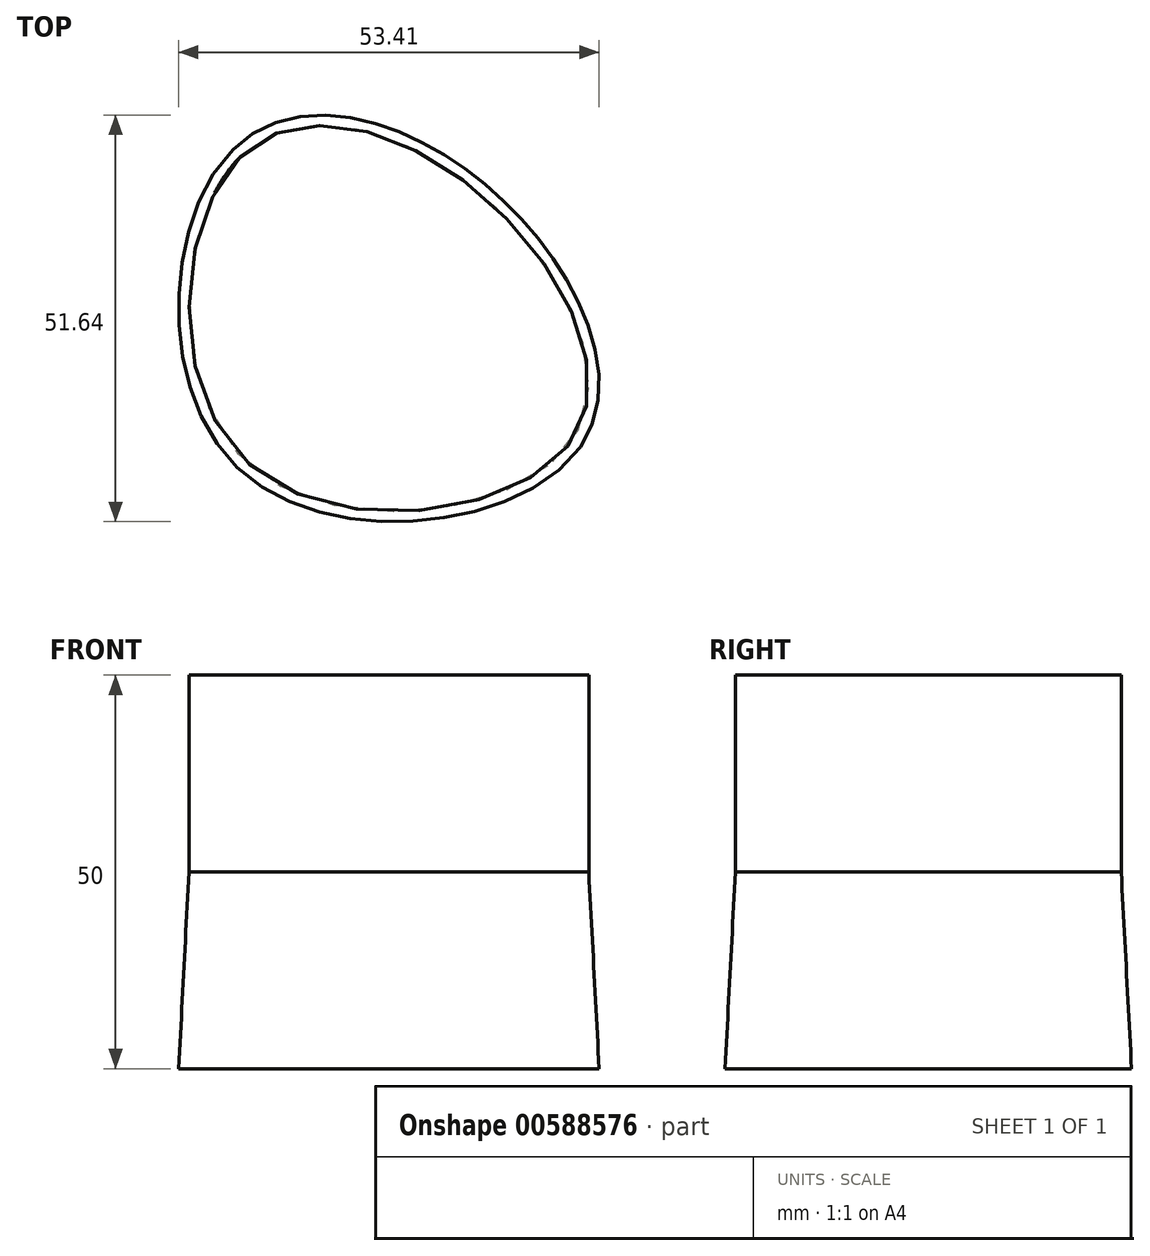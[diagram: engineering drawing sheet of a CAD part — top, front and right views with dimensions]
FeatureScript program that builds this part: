
annotation { "Feature Type Name" : "Feature", "Feature Type Description" : "" }
export const myFeature = defineFeature(function(context is Context, id is Id, definition is map)
    precondition{}
    {
        {
            var Q0;
            Q0=qCreatedBy(makeId("Top.planeOp"),FACE);
            var sketch = newSketch(context, id + "F0", { "sketchPlane" : qUnion([Q0])});
            skFitSpline(sketch, "E0", {"points": [v(-4.7, 13.57) * mm, v(-3.6, -25.48) * mm, v(37.42, -22.53) * mm, v(25.02, 9.52) * mm, v(-4.7, 13.57) * mm]});
            skSolve(sketch);
        }
        {
            var Q0;
            Q0 = qSketchRegion(id + "F0", true);
            extrude(context, id + "F1", {"entities" : qUnion([Q0]), "depth" : 25 * mm, "offsetDistance" : 25 * mm});
        }
        {
            var Q0;
            Q0=makeQuery(id+"F1.opExtrude","CAP_FACE",FACE,{"disambiguationData":[OSD([sQuery(id+"F0.wireOp",EDGE,"E0")])],"isStart":true});
            extrude(context, id + "F2", {"entities" : qUnion([Q0]), "operationType" : NewBodyOperationType.ADD, "depth" : 25 * mm, "offsetDistance" : 25 * mm, "hasDraft" : true, "draftAngle" : 3 * degree});
        }
    });
